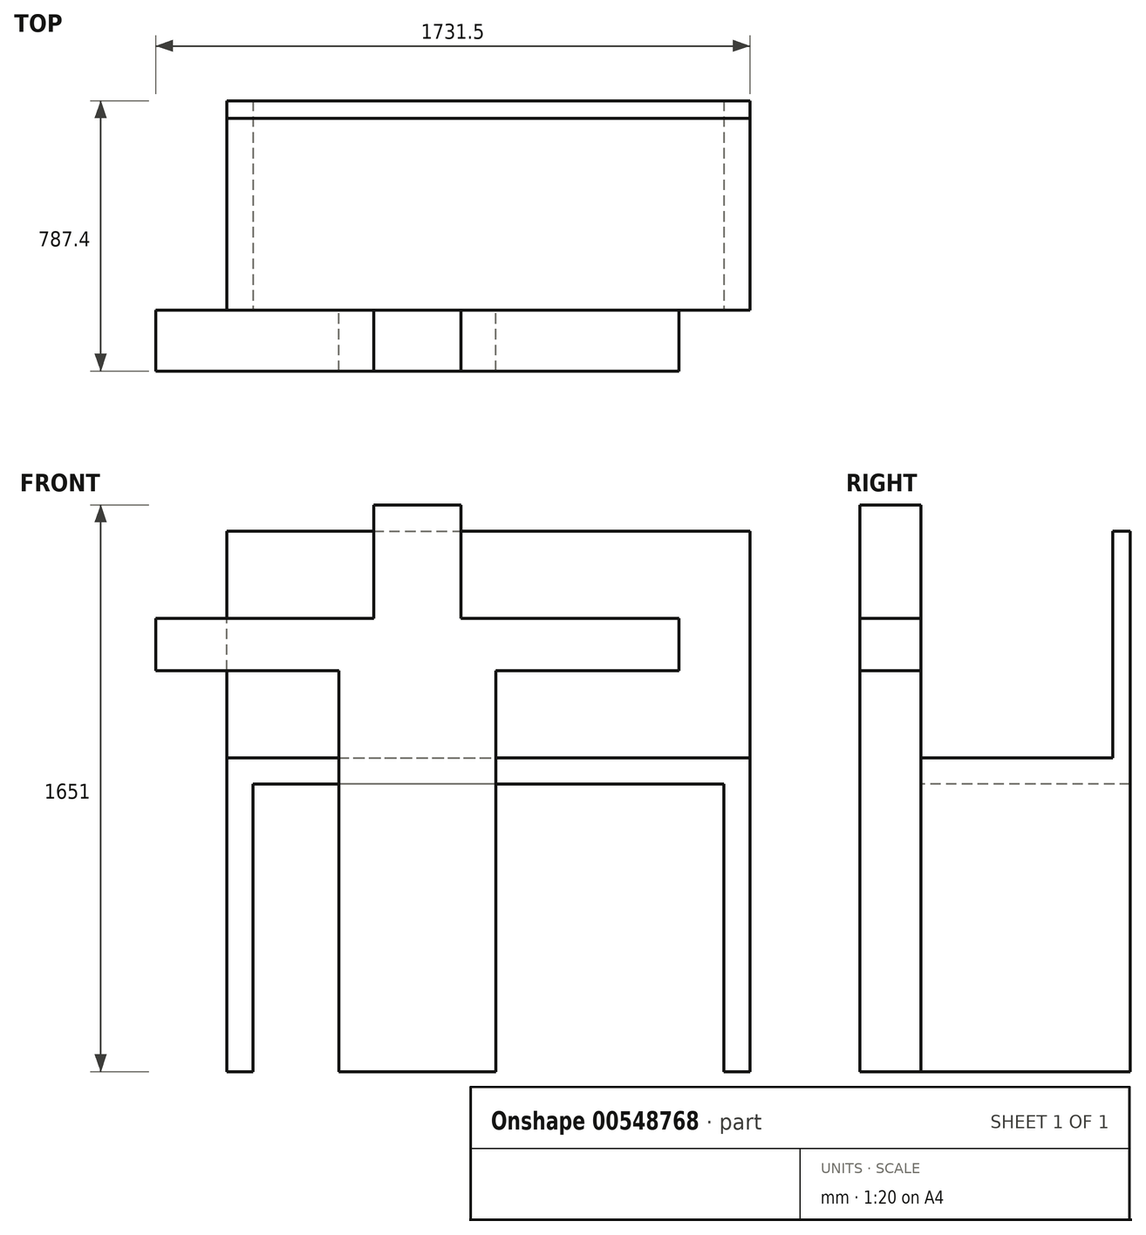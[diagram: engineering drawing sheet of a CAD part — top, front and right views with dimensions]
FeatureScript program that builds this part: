
annotation { "Feature Type Name" : "Feature", "Feature Type Description" : "" }
export const myFeature = defineFeature(function(context is Context, id is Id, definition is map)
    precondition{}
    {
        {
            var Q0;
            Q0=qCreatedBy(makeId("Front.planeOp"),FACE);
            var sketch = newSketch(context, id + "F0", { "sketchPlane" : qUnion([Q0])});
            skLineSegment(sketch, "E0", {"start": v(0, 0) * mm, "end": v(0, 914.4) * mm});
            skLineSegment(sketch, "E1", {"start": v(0, 914.4) * mm, "end": v(1524, 914.4) * mm});
            skLineSegment(sketch, "E2", {"start": v(1524, 914.4) * mm, "end": v(1524, 0) * mm});
            skLineSegment(sketch, "E3", {"start": v(1524, 0) * mm, "end": v(1447.8, 0) * mm});
            skLineSegment(sketch, "E4", {"start": v(1447.8, 0) * mm, "end": v(1447.8, 838.2) * mm});
            skLineSegment(sketch, "E5", {"start": v(1447.8, 838.2) * mm, "end": v(76.2, 838.2) * mm});
            skLineSegment(sketch, "E6", {"start": v(76.2, 838.2) * mm, "end": v(76.2, 0) * mm});
            skLineSegment(sketch, "E7", {"start": v(76.2, 0) * mm, "end": v(0, 0) * mm});
            skSolve(sketch);
        }
        {
            var Q0;
            Q0 = qSketchRegion(id + "F0", true);
            extrude(context, id + "F1", {"entities" : qUnion([Q0]), "oppositeDirection" : true, "depth" : 609.6 * mm, "offsetDistance" : 25.4 * mm});
        }
        {
            var Q0;
            Q0=makeQuery(id+"F1.opExtrude","SWEPT_FACE",FACE,{"disambiguationData":[OSD([sQuery(id+"F0.wireOp",EDGE,"E2")])]});
            var sketch = newSketch(context, id + "F2", { "sketchPlane" : qUnion([Q0])});
            skLineSegment(sketch, "E8", {"start": v(609.6, 914.4) * mm, "end": v(609.6, 1574.8) * mm});
            skLineSegment(sketch, "E9", {"start": v(609.6, 1574.8) * mm, "end": v(558.8, 1574.8) * mm});
            skLineSegment(sketch, "E10", {"start": v(558.8, 1574.8) * mm, "end": v(558.8, 914.4) * mm});
            skSolve(sketch);
        }
        {
            var Q0;
            {var subQ0=sQuery(id+"F2.wireOp",EDGE,"E8");Q0=makeQuery(id+"F2.imprint","IMPRINT",FACE,{"disambiguationData":[TD([[makeQuery(id+"F2.imprint","IMPRINT",EDGE,{"derivedFrom":subQ0}),1.0]])]});}
            var Q1;
            Q1=makeQuery(id+"F1.opExtrude","SWEPT_FACE",FACE,{"disambiguationData":[OSD([sQuery(id+"F0.wireOp",EDGE,"E0")])]});
            extrude(context, id + "F3", {"entities" : qUnion([Q0]), "operationType" : NewBodyOperationType.ADD, "endBound" : BoundingType.UP_TO_SURFACE, "oppositeDirection" : true, "depth" : 1066.8 * mm, "endBoundEntityFace" : qUnion([Q1]), "offsetDistance" : 25.4 * mm});
        }
        {
            var Q0;
            Q0=qCreatedBy(makeId("Front.planeOp"),FACE);
            var sketch = newSketch(context, id + "F4", { "sketchPlane" : qUnion([Q0])});
            skLineSegment(sketch, "E11", {"start": v(325.9, 0) * mm, "end": v(783.1, 0) * mm});
            skLineSegment(sketch, "E12", {"start": v(1316.5, 1320.8) * mm, "end": v(681.5, 1320.8) * mm});
            skLineSegment(sketch, "E13", {"start": v(681.5, 1320.8) * mm, "end": v(681.5, 1651) * mm});
            skLineSegment(sketch, "E14", {"start": v(681.5, 1651) * mm, "end": v(427.5, 1651) * mm});
            skLineSegment(sketch, "E15", {"start": v(427.5, 1651) * mm, "end": v(427.5, 1320.8) * mm});
            skLineSegment(sketch, "E16", {"start": v(427.5, 1320.8) * mm, "end": v(-207.5, 1320.8) * mm});
            skLineSegment(sketch, "E17", {"start": v(-207.5, 1320.8) * mm, "end": v(-207.5, 1168.4) * mm});
            skLineSegment(sketch, "E18", {"start": v(-207.5, 1168.4) * mm, "end": v(325.9, 1168.4) * mm});
            skLineSegment(sketch, "E19", {"start": v(325.9, 1168.4) * mm, "end": v(325.9, 0) * mm});
            skLineSegment(sketch, "E20", {"start": v(1316.5, 1320.8) * mm, "end": v(1316.5, 1168.4) * mm});
            skLineSegment(sketch, "E21", {"start": v(1316.5, 1168.4) * mm, "end": v(783.1, 1168.4) * mm});
            skLineSegment(sketch, "E22", {"start": v(783.1, 1168.4) * mm, "end": v(783.1, 0) * mm});
            skSolve(sketch);
        }
        {
            var Q0;
            Q0 = qSketchRegion(id + "F4", true);
            extrude(context, id + "F5", {"entities" : qUnion([Q0]), "depth" : 177.8 * mm, "offsetDistance" : 25.4 * mm});
        }
    });
